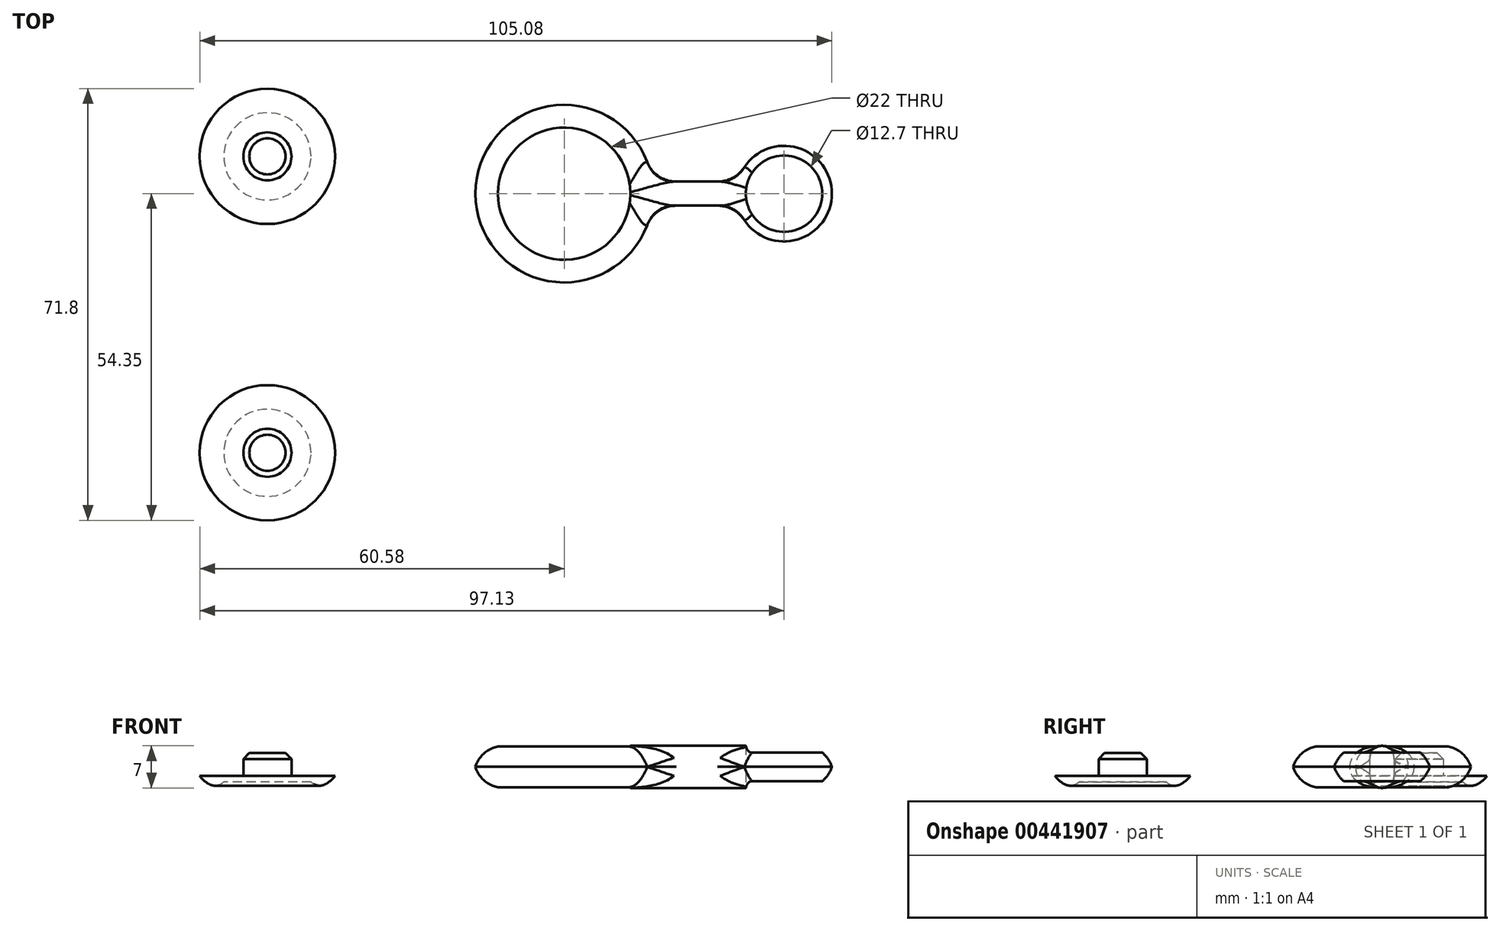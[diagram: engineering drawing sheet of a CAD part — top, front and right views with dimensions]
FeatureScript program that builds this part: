
annotation { "Feature Type Name" : "Feature", "Feature Type Description" : "" }
export const myFeature = defineFeature(function(context is Context, id is Id, definition is map)
    precondition{}
    {
        {
            var Q0;
            Q0=qCreatedBy(makeId("Top.planeOp"),FACE);
            var sketch = newSketch(context, id + "F0", { "sketchPlane" : qUnion([Q0])});
            skCircle(sketch, "E0", {"center": v(0, 0) * mm, "radius": 11 * mm});
            skArc(sketch, "E1.0", {"start": v(14.87, 2) * mm, "mid": v(-15, 0) * mm, "end": v(14.87, -2) * mm});
            skCircle(sketch, "E2", {"center": v(36.55, 0) * mm, "radius": 6.35 * mm});
            skArc(sketch, "E3", {"start": v(28.62, -2) * mm, "mid": v(44.73, 0) * mm, "end": v(28.62, 2) * mm});
            skLineSegment(sketch, "E4.0", {"start": v(14.87, -2) * mm, "end": v(28.62, -2) * mm});
            skLineSegment(sketch, "E5.0", {"start": v(14.87, 2) * mm, "end": v(28.62, 2) * mm});
            skSolve(sketch);
        }
        {
            var Q0;
            Q0=makeQuery(id+"F0.imprint","IMPRINT",FACE,{"disambiguationData":[TD([[makeQuery(id+"F0.imprint","IMPRINT",EDGE,{"derivedFrom":sQuery(id+"F0.wireOp",EDGE,"E0")}),-1.0]])]});
            extrude(context, id + "F1", {"entities" : qUnion([Q0]), "depth" : 7 * mm});
        }
        {
            var Q0;
            Q0=makeQuery(id+"F1.opExtrude","CAP_EDGE",EDGE,{"disambiguationData":[OSD([sQuery(id+"F0.wireOp",EDGE,"E1.0")])],"isStart":false});
            var Q1;
            Q1=makeQuery(id+"F1.opExtrude","CAP_EDGE",EDGE,{"disambiguationData":[OSD([sQuery(id+"F0.wireOp",EDGE,"E1.0")])],"isStart":true});
            var Q2;
            Q2=makeQuery(id+"F1.opExtrude","CAP_EDGE",EDGE,{"disambiguationData":[OSD([sQuery(id+"F0.wireOp",EDGE,"E3")])],"isStart":false});
            var Q3;
            Q3=makeQuery(id+"F1.opExtrude","CAP_EDGE",EDGE,{"disambiguationData":[OSD([sQuery(id+"F0.wireOp",EDGE,"E3")])],"isStart":true});
            fillet(context, id + "F2", {"entities" : qUnion([Q0, Q1, Q2, Q3]), "radius" : 5 * mm, "tangentPropagation" : true, "allowEdgeOverflow" : false});
        }
        {
            var Q0;
            Q0=makeQuery(id+"F1.opExtrude","CAP_EDGE",EDGE,{"disambiguationData":[OSD([sQuery(id+"F0.wireOp",EDGE,"E4.0")])],"isStart":false});
            var Q1;
            Q1=makeQuery(id+"F1.opExtrude","CAP_EDGE",EDGE,{"disambiguationData":[OSD([sQuery(id+"F0.wireOp",EDGE,"E5.0")])],"isStart":false});
            var Q2;
            Q2=makeQuery(id+"F1.opExtrude","CAP_EDGE",EDGE,{"disambiguationData":[OSD([sQuery(id+"F0.wireOp",EDGE,"E5.0")])],"isStart":true});
            var Q3;
            Q3=makeQuery(id+"F1.opExtrude","CAP_EDGE",EDGE,{"disambiguationData":[OSD([sQuery(id+"F0.wireOp",EDGE,"E4.0")])],"isStart":true});
            fillet(context, id + "F3", {"entities" : qUnion([Q0, Q1, Q2, Q3]), "radius" : 2 * mm, "allowEdgeOverflow" : false});
        }
        {
            var Q0;
            Q0=makeQuery(id+"F2.opFillet","BLEND_EDGE",EDGE,{"blendedFrom":[makeQuery(id+"F1.opExtrude","CAP_EDGE",EDGE,{"disambiguationData":[OSD([sQuery(id+"F0.wireOp",EDGE,"E1.0")])],"isStart":true}),makeQuery(id+"F1.opExtrude","SWEPT_FACE",FACE,{"disambiguationData":[OSD([sQuery(id+"F0.wireOp",EDGE,"E4.0")])]})],"blendedInto":[makeQuery(id+"F1.opExtrude","SWEPT_FACE",FACE,{"disambiguationData":[OSD([sQuery(id+"F0.wireOp",EDGE,"E4.0")])]})]});
            var Q1;
            Q1=makeQuery(id+"F2.opFillet","BLEND_EDGE",EDGE,{"blendedFrom":[makeQuery(id+"F1.opExtrude","CAP_EDGE",EDGE,{"disambiguationData":[OSD([sQuery(id+"F0.wireOp",EDGE,"E1.0")])],"isStart":false}),makeQuery(id+"F1.opExtrude","SWEPT_FACE",FACE,{"disambiguationData":[OSD([sQuery(id+"F0.wireOp",EDGE,"E4.0")])]})],"blendedInto":[makeQuery(id+"F1.opExtrude","SWEPT_FACE",FACE,{"disambiguationData":[OSD([sQuery(id+"F0.wireOp",EDGE,"E4.0")])]})]});
            var Q2;
            Q2=makeQuery(id+"F2.opFillet","BLEND_EDGE",EDGE,{"blendedFrom":[makeQuery(id+"F1.opExtrude","CAP_EDGE",EDGE,{"disambiguationData":[OSD([sQuery(id+"F0.wireOp",EDGE,"E1.0")])],"isStart":false}),makeQuery(id+"F1.opExtrude","SWEPT_FACE",FACE,{"disambiguationData":[OSD([sQuery(id+"F0.wireOp",EDGE,"E5.0")])]})],"blendedInto":[makeQuery(id+"F1.opExtrude","SWEPT_FACE",FACE,{"disambiguationData":[OSD([sQuery(id+"F0.wireOp",EDGE,"E5.0")])]})]});
            var Q3;
            Q3=makeQuery(id+"F2.opFillet","BLEND_EDGE",EDGE,{"blendedFrom":[makeQuery(id+"F1.opExtrude","CAP_EDGE",EDGE,{"disambiguationData":[OSD([sQuery(id+"F0.wireOp",EDGE,"E1.0")])],"isStart":true}),makeQuery(id+"F1.opExtrude","SWEPT_FACE",FACE,{"disambiguationData":[OSD([sQuery(id+"F0.wireOp",EDGE,"E5.0")])]})],"blendedInto":[makeQuery(id+"F1.opExtrude","SWEPT_FACE",FACE,{"disambiguationData":[OSD([sQuery(id+"F0.wireOp",EDGE,"E5.0")])]})]});
            var Q4;
            Q4=makeQuery(id+"F2.opFillet","BLEND_EDGE",EDGE,{"blendedFrom":[makeQuery(id+"F1.opExtrude","CAP_EDGE",EDGE,{"disambiguationData":[OSD([sQuery(id+"F0.wireOp",EDGE,"E3")])],"isStart":false}),makeQuery(id+"F1.opExtrude","SWEPT_FACE",FACE,{"disambiguationData":[OSD([sQuery(id+"F0.wireOp",EDGE,"E5.0")])]})],"blendedInto":[makeQuery(id+"F1.opExtrude","SWEPT_FACE",FACE,{"disambiguationData":[OSD([sQuery(id+"F0.wireOp",EDGE,"E5.0")])]})]});
            var Q5;
            Q5=makeQuery(id+"F2.opFillet","BLEND_EDGE",EDGE,{"blendedFrom":[makeQuery(id+"F1.opExtrude","CAP_EDGE",EDGE,{"disambiguationData":[OSD([sQuery(id+"F0.wireOp",EDGE,"E3")])],"isStart":true}),makeQuery(id+"F1.opExtrude","SWEPT_FACE",FACE,{"disambiguationData":[OSD([sQuery(id+"F0.wireOp",EDGE,"E5.0")])]})],"blendedInto":[makeQuery(id+"F1.opExtrude","SWEPT_FACE",FACE,{"disambiguationData":[OSD([sQuery(id+"F0.wireOp",EDGE,"E5.0")])]})]});
            var Q6;
            Q6=makeQuery(id+"F2.opFillet","BLEND_EDGE",EDGE,{"blendedFrom":[makeQuery(id+"F1.opExtrude","CAP_EDGE",EDGE,{"disambiguationData":[OSD([sQuery(id+"F0.wireOp",EDGE,"E3")])],"isStart":false}),makeQuery(id+"F1.opExtrude","SWEPT_FACE",FACE,{"disambiguationData":[OSD([sQuery(id+"F0.wireOp",EDGE,"E4.0")])]})],"blendedInto":[makeQuery(id+"F1.opExtrude","SWEPT_FACE",FACE,{"disambiguationData":[OSD([sQuery(id+"F0.wireOp",EDGE,"E4.0")])]})]});
            var Q7;
            Q7=makeQuery(id+"F2.opFillet","BLEND_EDGE",EDGE,{"blendedFrom":[makeQuery(id+"F1.opExtrude","CAP_EDGE",EDGE,{"disambiguationData":[OSD([sQuery(id+"F0.wireOp",EDGE,"E3")])],"isStart":true}),makeQuery(id+"F1.opExtrude","SWEPT_FACE",FACE,{"disambiguationData":[OSD([sQuery(id+"F0.wireOp",EDGE,"E4.0")])]})],"blendedInto":[makeQuery(id+"F1.opExtrude","SWEPT_FACE",FACE,{"disambiguationData":[OSD([sQuery(id+"F0.wireOp",EDGE,"E4.0")])]})]});
            fillet(context, id + "F4", {"entities" : qUnion([Q0, Q1, Q2, Q3, Q4, Q5, Q6, Q7]), "radius" : 5 * mm, "tangentPropagation" : true, "allowEdgeOverflow" : false});
        }
        {
            var Q0;
            Q0=qCreatedBy(makeId("Top.planeOp"),FACE);
            var sketch = newSketch(context, id + "F5", { "sketchPlane" : qUnion([Q0])});
            skCircle(sketch, "E6", {"center": v(-49.33, 6.2) * mm, "radius": 11.25 * mm});
            skSolve(sketch);
        }
        {
            var Q0;
            Q0=makeQuery(id+"F5.imprint","IMPRINT",FACE,{"disambiguationData":[TD([[makeQuery(id+"F5.imprint","IMPRINT",EDGE,{"derivedFrom":sQuery(id+"F5.wireOp",EDGE,"E6")}),1.0]])]});
            extrude(context, id + "F6", {"entities" : qUnion([Q0]), "depth" : 2 * mm});
        }
        {
            var Q0;
            Q0=makeQuery(id+"F6.opExtrude","CAP_FACE",FACE,{"disambiguationData":[OSD([sQuery(id+"F5.wireOp",EDGE,"E6")])],"isStart":false});
            var sketch = newSketch(context, id + "F7", { "sketchPlane" : qUnion([Q0])});
            skCircle(sketch, "E7", {"center": v(-49.33, 6.2) * mm, "radius": 4 * mm});
            skSolve(sketch);
        }
        {
            var Q0;
            Q0=makeQuery(id+"F7.imprint","IMPRINT",FACE,{"disambiguationData":[TD([[makeQuery(id+"F7.imprint","IMPRINT",EDGE,{"derivedFrom":sQuery(id+"F7.wireOp",EDGE,"E7")}),1.0]])]});
            extrude(context, id + "F8", {"entities" : qUnion([Q0]), "operationType" : NewBodyOperationType.ADD, "depth" : 3.8 * mm});
        }
        {
            var Q0;
            Q0=makeQuery(id+"F8.opExtrude","CAP_EDGE",EDGE,{"disambiguationData":[OSD([sQuery(id+"F7.wireOp",EDGE,"E7")])],"isStart":false});
            chamfer(context, id + "F9", {"entities" : qUnion([Q0]), "width" : 1 * mm, "tangentPropagation" : true});
        }
        {
            var Q0;
            Q0=makeQuery(id+"F6.opExtrude","CAP_EDGE",EDGE,{"disambiguationData":[OSD([sQuery(id+"F5.wireOp",EDGE,"E6")])],"isStart":true});
            fillet(context, id + "F10", {"entities" : qUnion([Q0]), "radius" : 5 * mm, "tangentPropagation" : true, "allowEdgeOverflow" : false});
        }
        {
            var Q0;
            Q0=makeQuery(id+"F6.opExtrude","CAP_FACE",FACE,{"disambiguationData":[OSD([sQuery(id+"F5.wireOp",EDGE,"E6")])],"isStart":true});
            extrude(context, id + "F11", {"entities" : qUnion([Q0]), "operationType" : NewBodyOperationType.REMOVE, "oppositeDirection" : true, "depth" : 1 * mm});
        }
        {
            var Q0;
            {var subQ0=sQuery(id+"F5.wireOp",EDGE,"E6");Q0=makeQuery(id+"F11.boolean.opBoolean","MERGE",EDGE,{"derivedFrom":[makeQuery(id+"F10.opFillet","BLEND_EDGE",EDGE,{"blendedFrom":[makeQuery(id+"F6.opExtrude","CAP_EDGE",EDGE,{"disambiguationData":[OSD([subQ0])],"isStart":true}),makeQuery(id+"F6.opExtrude","CAP_FACE",FACE,{"disambiguationData":[OSD([subQ0])],"isStart":true})],"blendedInto":[makeQuery(id+"F6.opExtrude","CAP_FACE",FACE,{"disambiguationData":[OSD([subQ0])],"isStart":true})]}),makeQuery(id+"F11.opExtrude","CAP_EDGE",EDGE,{"disambiguationData":[OSD([subQ0])],"isStart":true})]});}
            fillet(context, id + "F12", {"entities" : qUnion([Q0]), "radius" : 2 * mm, "tangentPropagation" : true, "allowEdgeOverflow" : false});
        }
        {
            var Q0;
            Q0=makeQuery(id+"F6.opExtrude","SWEPT_BODY",BODY,{"disambiguationData":[OSD([sQuery(id+"F5.wireOp",EDGE,"E6")])]});
            transform(context, id + "F13", {"entities" : qUnion([Q0]), "transformType" : TransformType.TRANSLATION_3D, "dx" : 0 * mm, "dy" : -49.3 * mm, "dz" : 0 * mm, "makeCopy" : true});
        }
    });
